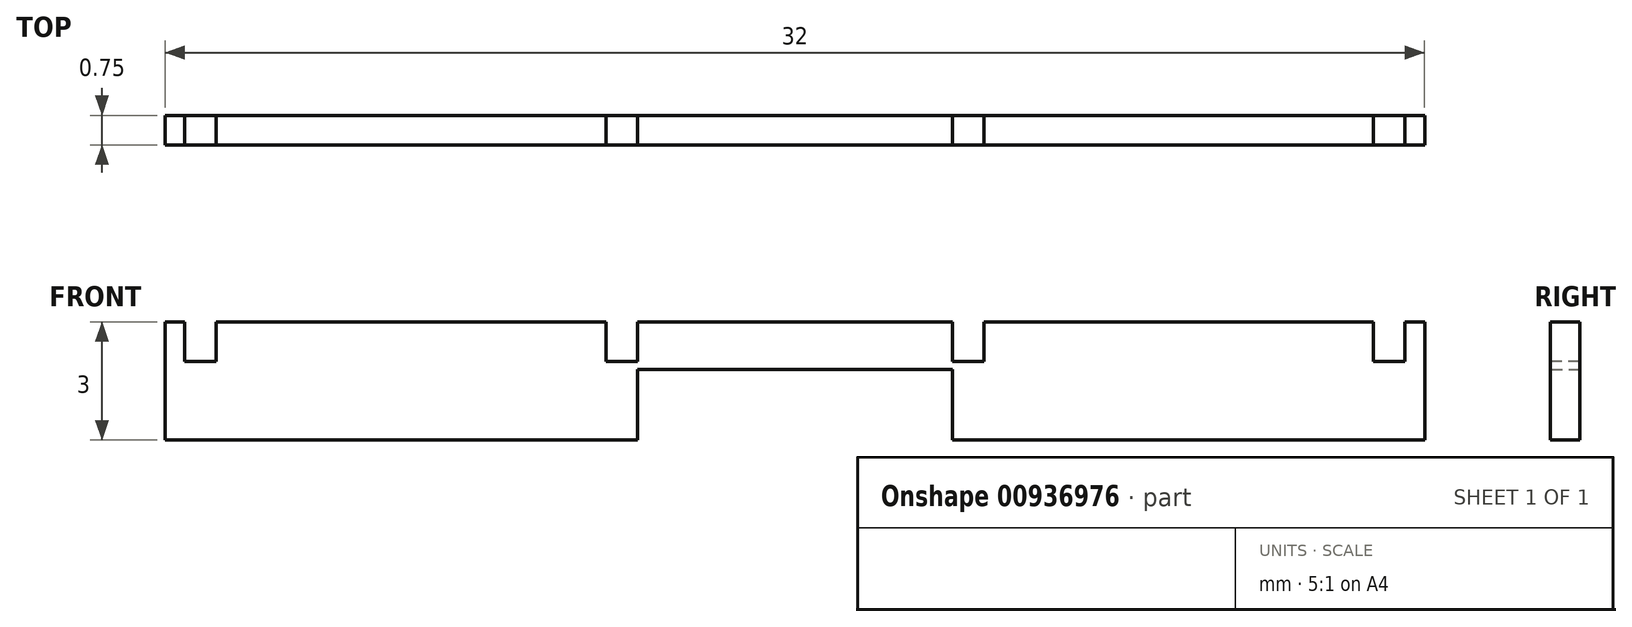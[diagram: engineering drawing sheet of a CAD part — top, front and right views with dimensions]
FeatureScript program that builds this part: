
annotation { "Feature Type Name" : "Feature", "Feature Type Description" : "" }
export const myFeature = defineFeature(function(context is Context, id is Id, definition is map)
    precondition{}
    {
        {
            var Q0;
            Q0=qCreatedBy(makeId("Front.planeOp"),FACE);
            var sketch = newSketch(context, id + "F0", { "sketchPlane" : qUnion([Q0])});
            skLineSegment(sketch, "E0", {"start": v(-20.15, 0) * mm, "end": v(11.85, 0) * mm});
            skLineSegment(sketch, "E1", {"start": v(11.85, -3) * mm, "end": v(-0.15, -3) * mm});
            skLineSegment(sketch, "E2", {"start": v(-0.15, -3) * mm, "end": v(-0.15, -1.2) * mm});
            skLineSegment(sketch, "E3", {"start": v(-0.15, -1.2) * mm, "end": v(-8.15, -1.2) * mm});
            skLineSegment(sketch, "E4", {"start": v(-8.15, -1.2) * mm, "end": v(-8.15, -3) * mm});
            skLineSegment(sketch, "E5", {"start": v(-8.15, -3) * mm, "end": v(-20.15, -3) * mm});
            skLineSegment(sketch, "E6", {"start": v(11.85, 0) * mm, "end": v(11.85, -3) * mm});
            skLineSegment(sketch, "E7", {"start": v(-20.15, -3) * mm, "end": v(-20.15, 0) * mm});
            skPoint(sketch, "E8.end.orphan", {"position": v(-20.15, 0) * mm});
            skSolve(sketch);
        }
        {
            var Q0;
            Q0=makeQuery(id+"F0.imprint","IMPRINT",FACE,{"disambiguationData":[TD([[makeQuery(id+"F0.imprint","IMPRINT",EDGE,{"derivedFrom":sQuery(id+"F0.wireOp",EDGE,"E0")}),-1.0]])]});
            extrude(context, id + "F1", {"entities" : qUnion([Q0]), "depth" : .75 * mm, "offsetDistance" : 25 * mm});
        }
        {
            var Q0;
            Q0=makeQuery(id+"F1.opExtrude","CAP_FACE",FACE,{"disambiguationData":[OSD([sQuery(id+"F0.wireOp",EDGE,"E0"),sQuery(id+"F0.wireOp",EDGE,"E1"),sQuery(id+"F0.wireOp",EDGE,"E2"),sQuery(id+"F0.wireOp",EDGE,"E3"),sQuery(id+"F0.wireOp",EDGE,"E4"),sQuery(id+"F0.wireOp",EDGE,"E5"),sQuery(id+"F0.wireOp",EDGE,"E8"),sQuery(id+"F0.wireOp",EDGE,"E6")])],"isStart":false});
            var sketch = newSketch(context, id + "F2", { "sketchPlane" : qUnion([Q0])});
            skLineSegment(sketch, "E9", {"start": v(-19.65, 0) * mm, "end": v(-19.65, -1) * mm});
            skLineSegment(sketch, "E10", {"start": v(-19.65, -1) * mm, "end": v(-18.85, -1) * mm});
            skLineSegment(sketch, "E11", {"start": v(-18.85, -1) * mm, "end": v(-18.85, 0) * mm});
            skSolve(sketch);
        }
        {
            var Q0;
            Q0 = qSketchRegion(id + "F2", true);
            var Q1;
            {var subQ0=sQuery(id+"F2.wireOp",EDGE,"E9");Q1=makeQuery(id+"F2.imprint","IMPRINT",FACE,{"disambiguationData":[TD([[makeQuery(id+"F2.imprint","IMPRINT",EDGE,{"derivedFrom":subQ0}),1.0]])]});}
            extrude(context, id + "F3", {"entities" : qUnion([Q0, Q1]), "operationType" : NewBodyOperationType.REMOVE, "endBound" : BoundingType.THROUGH_ALL, "oppositeDirection" : true, "depth" : 25 * mm, "offsetDistance" : 25 * mm});
        }
        {
            var Q0;
            Q0=makeQuery(id+"F1.opExtrude","CAP_FACE",FACE,{"disambiguationData":[OSD([sQuery(id+"F0.wireOp",EDGE,"E0"),sQuery(id+"F0.wireOp",EDGE,"E1"),sQuery(id+"F0.wireOp",EDGE,"E2"),sQuery(id+"F0.wireOp",EDGE,"E3"),sQuery(id+"F0.wireOp",EDGE,"E4"),sQuery(id+"F0.wireOp",EDGE,"E5"),sQuery(id+"F0.wireOp",EDGE,"E8"),sQuery(id+"F0.wireOp",EDGE,"E6")])],"isStart":false});
            var sketch = newSketch(context, id + "F4", { "sketchPlane" : qUnion([Q0])});
            skLineSegment(sketch, "E12", {"start": v(-8.95, 0) * mm, "end": v(-8.95, -1) * mm});
            skLineSegment(sketch, "E13", {"start": v(-8.95, -1) * mm, "end": v(-8.15, -1) * mm});
            skLineSegment(sketch, "E14", {"start": v(-8.15, -1) * mm, "end": v(-8.15, 0) * mm});
            skSolve(sketch);
        }
        {
            var Q0;
            Q0 = qSketchRegion(id + "F4", true);
            var Q1;
            {var subQ0=sQuery(id+"F4.wireOp",EDGE,"E12");Q1=makeQuery(id+"F4.imprint","IMPRINT",FACE,{"disambiguationData":[TD([[makeQuery(id+"F4.imprint","IMPRINT",EDGE,{"derivedFrom":subQ0}),1.0]])]});}
            extrude(context, id + "F5", {"entities" : qUnion([Q0, Q1]), "operationType" : NewBodyOperationType.REMOVE, "endBound" : BoundingType.THROUGH_ALL, "oppositeDirection" : true, "depth" : 25 * mm, "offsetDistance" : 25 * mm});
        }
        {
            var Q0;
            Q0=makeQuery(id+"F1.opExtrude","CAP_FACE",FACE,{"disambiguationData":[OSD([sQuery(id+"F0.wireOp",EDGE,"E0"),sQuery(id+"F0.wireOp",EDGE,"E1"),sQuery(id+"F0.wireOp",EDGE,"E2"),sQuery(id+"F0.wireOp",EDGE,"E3"),sQuery(id+"F0.wireOp",EDGE,"E4"),sQuery(id+"F0.wireOp",EDGE,"E5"),sQuery(id+"F0.wireOp",EDGE,"E8"),sQuery(id+"F0.wireOp",EDGE,"E6")])],"isStart":false});
            var sketch = newSketch(context, id + "F6", { "sketchPlane" : qUnion([Q0])});
            skLineSegment(sketch, "E15", {"start": v(-0.15, 0) * mm, "end": v(-0.15, -1) * mm});
            skLineSegment(sketch, "E16", {"start": v(-0.15, -1) * mm, "end": v(0.65, -1) * mm});
            skLineSegment(sketch, "E17", {"start": v(0.65, -1) * mm, "end": v(0.65, 0) * mm});
            skSolve(sketch);
        }
        {
            var Q0;
            Q0 = qSketchRegion(id + "F6", true);
            var Q1;
            {var subQ0=sQuery(id+"F6.wireOp",EDGE,"E15");Q1=makeQuery(id+"F6.imprint","IMPRINT",FACE,{"disambiguationData":[TD([[makeQuery(id+"F6.imprint","IMPRINT",EDGE,{"derivedFrom":subQ0}),1.0]])]});}
            extrude(context, id + "F7", {"entities" : qUnion([Q0, Q1]), "operationType" : NewBodyOperationType.REMOVE, "endBound" : BoundingType.THROUGH_ALL, "oppositeDirection" : true, "depth" : 25 * mm, "offsetDistance" : 25 * mm});
        }
        {
            var Q0;
            Q0=makeQuery(id+"F1.opExtrude","CAP_FACE",FACE,{"disambiguationData":[OSD([sQuery(id+"F0.wireOp",EDGE,"E0"),sQuery(id+"F0.wireOp",EDGE,"E1"),sQuery(id+"F0.wireOp",EDGE,"E2"),sQuery(id+"F0.wireOp",EDGE,"E3"),sQuery(id+"F0.wireOp",EDGE,"E4"),sQuery(id+"F0.wireOp",EDGE,"E5"),sQuery(id+"F0.wireOp",EDGE,"E6"),sQuery(id+"F0.wireOp",EDGE,"E7")])],"isStart":false});
            var sketch = newSketch(context, id + "F8", { "sketchPlane" : qUnion([Q0])});
            skLineSegment(sketch, "E18", {"start": v(10.55, 0) * mm, "end": v(10.55, -1) * mm});
            skLineSegment(sketch, "E19", {"start": v(10.55, -1) * mm, "end": v(11.35, -1) * mm});
            skLineSegment(sketch, "E20", {"start": v(11.35, -1) * mm, "end": v(11.35, 0) * mm});
            skSolve(sketch);
        }
        {
            var Q0;
            Q0 = qSketchRegion(id + "F8", true);
            var Q1;
            {var subQ0=sQuery(id+"F8.wireOp",EDGE,"E18");Q1=makeQuery(id+"F8.imprint","IMPRINT",FACE,{"disambiguationData":[TD([[makeQuery(id+"F8.imprint","IMPRINT",EDGE,{"derivedFrom":subQ0}),1.0]])]});}
            extrude(context, id + "F9", {"entities" : qUnion([Q0, Q1]), "operationType" : NewBodyOperationType.REMOVE, "endBound" : BoundingType.THROUGH_ALL, "oppositeDirection" : true, "depth" : 25 * mm, "offsetDistance" : 25 * mm});
        }
    });
